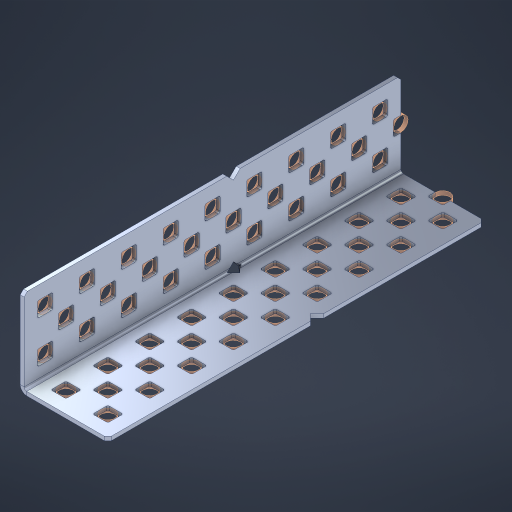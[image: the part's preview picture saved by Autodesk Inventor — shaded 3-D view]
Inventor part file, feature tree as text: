
AUTODESK INVENTOR PART (.ipt)
format: ipt  version: 2023 (Build 270158000, 158)  size: 897,024 bytes
history: native  units: in
note: dims shown in document units (in); Inventor stores cm internally (conversion verified against a paired STEP export)
features: other x60, extrude x52, sheet_metal_op x8, sketch x7, pattern_linear x2, mirror x1, chamfer x1
ambient origin geometry x8: Origin, YZ Plane, XZ Plane, XY Plane, X Axis, Y Axis, Z Axis, Center Point
bodies: Solid1 (feature_tree), Body (feature_tree)
feature tree (131):
  sheet_metal_op  "Flanges"
  sheet_metal_op  "Body Pattern"
  pattern_linear  "Center Pattern"  Spacing1=1.0in  [1 undecoded]
  other  "Arc Length"
  pattern_linear  "Notch Pattern"  Spacing1=0.1875in  [1 undecoded]
  other  "Diagonal Plane"
  mirror  "Everything Mirrored"
  chamfer  "End Chamfer"
  sketch  "Sketch1"  dims[d0=1.0in]
  other  "Plate1"
  sketch  "Sketch2"  dims[d1=4.5in]
  other  "Plate2"
  sheet_metal_op  "Bend1"
  sheet_metal_op  "Corner1"
  sketch  "Sketch8"  dims[d2=0.0469in]
  sketch  "Sketch9"  dims[d3=0.0469in]
  other  "Srf91"
  sheet_metal_op  "Body Pattern Sketch"
  other  "Srf92"
  sketch  "Sketch13"  dims[d4=0.0234in]
  sketch  "Sketch15"  dims[d5=0.0938in]
  sketch  "Sketch16"  dims[d6=0.0469in d7=1.0in d8=90.0deg d9=0.0312in d10=0.1875in d11=0.0469in d12=0.0469in d49=0.182in d50=0.02in d52=0.25in d53=0.0469in d54=0.0in d55=0.172in d56=1.0in d57=0.0in d60=3.5433in d62=0.5in d63=0.7874in d65=0.5in d85=0.1473in d86=0.1659in d89=0.0469in d90=0.0in d91=0.04in d92=0.0491in d95=2.5in d96=0.04in d97=0.25in d98=45.0deg d99=0.25in d106=0.182in d107=0.02in d108=0.5in d110=0.0469in d111=0.0in d112=0.172in d113=0.5in d114=0.0in d117=0.5in d123=0.25in d125=0.25in d126=0.0491in d127=0.1227in d128=0.08in d129=0.04in d130=2.5in]
  other  "Srf786"
  other  "Srf856"
  other  "Srf857"
  other  "Srf858"
  other  "Srf859"
  other  "Srf860"
  other  "Srf861"
  other  "Srf889"
  other  "Srf890"
  other  "Srf891"
  other  "Srf1275"
  other  "Srf1276"
  other  "Srf1278"
  other  "Srf1279"
  other  "Srf1280"
  other  "Srf1281"
  other  "Srf1282"
  other  "Srf1283"
  other  "Srf1277"
  other  "Srf1285"
  other  "Srf1286"
  other  "Srf1287"
  other  "Srf1383"
  other  "Srf1384"
  other  "Srf1385"
  other  "Srf1386"
  other  "Srf1387"
  other  "Srf1388"
  other  "Srf1389"
  other  "Srf1390"
  other  "Srf1391"
  other  "Srf1392"
  other  "Srf1445"
  other  "Srf1446"
  other  "Srf1447"
  other  "Srf1448"
  other  "Srf1449"
  other  "Srf1475"
  other  "Srf1476"
  other  "Srf1477"
  other  "Srf1478"
  other  "Srf1479"
  other  "Srf1480"
  other  "Srf1481"
  other  "Srf1482"
  other  "Srf1483"
  other  "Srf1484"
  other  "Srf1537"
  other  "Srf1538"
  other  "Srf1539"
  other  "Srf1540"
  other  "Srf1541"
  sheet_metal_op  "Body Stamp"
  sheet_metal_op  "Body Circle"
  other  "Center Stamp"
  other  "Center Circle"
  sheet_metal_op  "Notch"
  extrude  "ExtrusionSrf92"  Depth=0.0469in
  extrude  "ExtrusionSrf856"  Depth=0.0469in
  extrude  "ExtrusionSrf857"  Depth=0.182in
  extrude  "ExtrusionSrf858"  Depth=0.02in
  extrude  "ExtrusionSrf859"  Depth=0.25in
  extrude  "ExtrusionSrf860"  Depth=0.0469in
  extrude  "ExtrusionSrf861"  TaperAngle=0.0deg  [1 undecoded]
  extrude  "ExtrusionSrf889"  Depth=2.5in
  extrude  "ExtrusionSrf890"  Depth=1.0in TaperAngle=0.0deg
  extrude  "ExtrusionSrf891"  Depth=2.5in
  extrude  "ExtrusionSrf1275"  Depth=0.5in
  extrude  "ExtrusionSrf1276"  Depth=2.5in
  extrude  "ExtrusionSrf1277"  Depth=2.5in
  extrude  "ExtrusionSrf1278"  Depth=0.0469in
  extrude  "ExtrusionSrf1279"  Depth=2.5in TaperAngle=0.0deg
  extrude  "ExtrusionSrf1280"  Depth=2.5in
  extrude  "ExtrusionSrf1281"  Depth=0.25in TaperAngle=45.0deg
  extrude  "ExtrusionSrf1282"  Depth=0.25in
  extrude  "ExtrusionSrf1345"  Depth=0.182in
  extrude  "ExtrusionSrf1346"  Depth=0.02in
  extrude  "ExtrusionSrf1347"  Depth=0.5in
  extrude  "ExtrusionSrf1348"  Depth=0.0469in
  extrude  "ExtrusionSrf1383"  TaperAngle=0.0deg  [1 undecoded]
  extrude  "ExtrusionSrf1384"  Depth=2.5in
  extrude  "ExtrusionSrf1385"  Depth=0.5in TaperAngle=0.0deg
  extrude  "ExtrusionSrf1386"  Depth=0.5in
  extrude  "ExtrusionSrf1387"  Depth=0.25in
  extrude  "ExtrusionSrf1388"  Depth=0.25in
  extrude  "ExtrusionSrf1389"  Depth=2.5in
  extrude  "ExtrusionSrf1390"  Depth=2.5in
  extrude  "ExtrusionSrf1391"  Depth=2.5in
  extrude  "ExtrusionSrf1392"  Depth=2.5in
  extrude  "ExtrusionSrf1445"  Depth=2.5in
  extrude  "ExtrusionSrf1446"  [1 undecoded]
  extrude  "ExtrusionSrf1447"  [1 undecoded]
  extrude  "ExtrusionSrf1448"  [1 undecoded]
  extrude  "ExtrusionSrf1449"  [1 undecoded]
  extrude  "ExtrusionSrf1475"  [1 undecoded]
  extrude  "ExtrusionSrf1476"  [1 undecoded]
  extrude  "ExtrusionSrf1477"  [1 undecoded]
  extrude  "ExtrusionSrf1478"  [1 undecoded]
  extrude  "ExtrusionSrf1479"  [1 undecoded]
  extrude  "ExtrusionSrf1480"  [1 undecoded]
  extrude  "ExtrusionSrf1481"  [1 undecoded]
  extrude  "ExtrusionSrf1482"  [1 undecoded]
  extrude  "ExtrusionSrf1483"  [1 undecoded]
  extrude  "ExtrusionSrf1484"  [1 undecoded]
  extrude  "ExtrusionSrf1537"  [1 undecoded]
  extrude  "ExtrusionSrf1538"  [1 undecoded]
  extrude  "ExtrusionSrf1539"  [1 undecoded]
  extrude  "ExtrusionSrf1540"  [1 undecoded]
  extrude  "ExtrusionSrf1541"  [1 undecoded]
note: 23 required parameter values undecoded (feature->parameter linkage not recoverable at this tier; creation-order binding heuristic only, values carry confidence <= 0.55)
